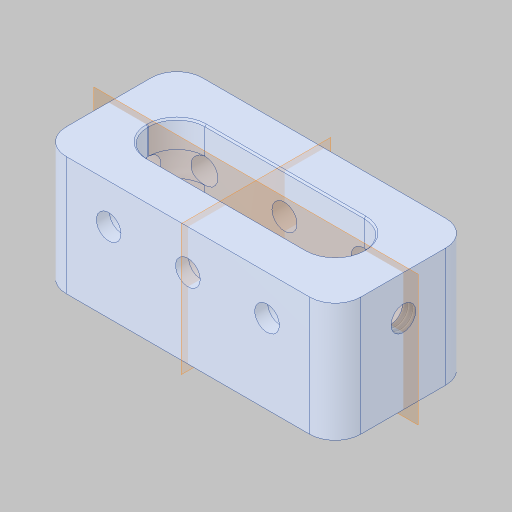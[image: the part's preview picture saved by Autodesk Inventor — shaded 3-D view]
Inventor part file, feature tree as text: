
AUTODESK INVENTOR PART (.ipt)
format: ipt  version: 2023.5 (Build 275446000, 446)  size: 454,144 bytes
history: native  units: in
note: dims shown in document units (in); Inventor stores cm internally (conversion verified against a paired STEP export)
features: sketch x4, hole x3, projected_geometry x2, extrude x1, chamfer x1
ambient origin geometry x8: Origin, YZ Plane, XZ Plane, XY Plane, X Axis, Y Axis, Z Axis, Center Point
bodies: Solid1 (feature_tree)
feature tree (11):
  extrude  "Extrusion1"  Depth=1.0in TaperAngle=0.0deg
  hole  "Hole1"  [1 undecoded]
  hole  "Hole2"  [1 undecoded]
  hole  "Hole3"  [1 undecoded]
  sketch  "Sketch1"  dims[d0=0.0625in d1=1.0in d2=0.0in]
  projected_geometry  "Projected Loop1"
  sketch  "Sketch2"  dims[d3=0.156in d4=0.38in d5=0.385in d6=0.25in d7=0.563in d8=1.0in d9=0.8108in]
  projected_geometry  "Projected Loop2"
  sketch  "Sketch3"  dims[d10=0.196in d11=0.5in d12=0.375in d13=0.25in d14=0.5635in d15=1.0in d16=0.8108in]
  sketch  "Sketch4"  dims[d17=0.156in d18=0.38in d19=0.385in d20=0.25in d21=0.563in d22=1.0in d23=0.8108in]
  chamfer  "Chamfer2"  [1 undecoded]
note: 4 required parameter values undecoded (feature->parameter linkage not recoverable at this tier; creation-order binding heuristic only, values carry confidence <= 0.55)
